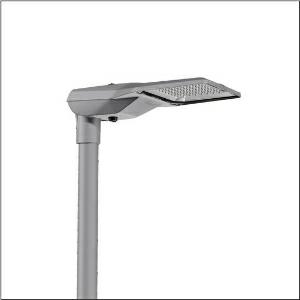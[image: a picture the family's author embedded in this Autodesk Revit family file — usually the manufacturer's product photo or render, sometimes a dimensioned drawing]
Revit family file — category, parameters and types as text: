
# Revit family: streetlight_sl_21_midi___st0_8a_5xe3c43t08lb_a4d4
name_source: partatom
category: Lighting Fixtures
units: mm (PartAtom-declared; Revit-internal decimal feet)

## family parameters
Cut with Voids When Loaded = No
Host = Face
Light Source = No
Part Type = Normal
Room Calculation Point = No
Round Connector Dimension = Use Diameter
Shared = No

## types (1)
- --- (1 x LED, 14950 lm, 99.6 W, 4000K)
    Apparent Load = 100 VA
    CIE Flux Codes = 38 75 97 100 100
    Color Rendering = 70
    Color Temperature = 4000K
    Default Elevation = 1800 mm
    Description = Streetlight SL 21 midi, mast luminaire, primary light control with lens, of PMMA, primary optical cover: cover, of toughened safety glass, transparent, light distribution: ST0.8a, light emission: direct distribution, primary light characteristic: asymmetric, installation type: side-entry, post-top, LED, High Power LED, rated luminous flux: 14.950lm, luminous efficacy: 150lm/W, light colour: 740, colour temperature: 4000K, control gear: D4i, control: overheat protection, constant luminous flux control, time-dependent luminous flux control, flexible luminous flux parameterisation, pre-setting: logarithmic dimming characteristic, mains connection: 230..240V, AC, 50/60Hz, start of lifetime: 100W, end of service life: 102W, reduction: 46W, luminaire housing, of diecast aluminium, powder-coated, Siteco® metallic grey (DB 702S), corrosivity category C5 mid according to DIN EN ISO 12944, please order mast flange separately, inclination adjustable: 0°, 5°, 10°, 15°, sealing non-destructively replaceable, multi-level sealing system, length: 644mm, width: 335mm, height: 110mm, mast flange for spigot size: 42mm (side-entry): 5XC10008XM4, 60/48mm (side-entry/post-top): 5XC10108XM2, 76/60mm (side-entry/post-top): 5XC10108XM1, mounting height: 4..8m, Smart Interface below and above, protection rating (complete): IP66, insulation class (complete): insulation class II (safety insulation), certification: CE, ENEC, ENEC+, VDE, impact resistance: IK10, permissible operating ambient temperature for outdoor applications: -40..+50°C, standard-compliant lighting for roads and squares, packaging unit: 1 piece

Light Distribution: ST0.8a
    Height = 111 mm
    Lamp = 1 x LED
    Lamp Light Flux = 14950 lm
    Lamp Power = 99.6 W
    Lamp count = 1
    Length = 644 mm
    Luminous efficacy = 150 lm/W
    Manufacturer = Siteco
    ModVariant = No
    Model = 5XE3C43T08LB
    Number of Poles = 1
    OnlyDefault = Yes
    Power Factor = 1
    Product Name = Streetlight SL 21 midi | ST0.8a
    Product group = mast luminaire | pylon top
    ProductGroupID = 6100
    Protection Class = Protection class II
    Protection Degree = IP 66
    RLX_Detail_Level = 1
    RLX_Emergency_Light_Flux = 0 lm
    RLX_Emergency_Type = 0
    RLX_Emergency_Type_DB = No
    RlxData = <blob elided: 26957 chars, md5=c2792af1>
    Socket = socket
    Standby Power = 0 W
    System Light Flux = 14950 lm
    System Power = 100 W
    Type Comments = factory setting: luminous flux: 100 % | dim-lin: 254 | 1020 mA
    Type Image = l_1004304.jpg
    URL = http://relux.com
    VarID = @adj_011377
    Voltage = 0 V
    Weight = 0.00 kg
    Width = 336 mm

## geometry (parser evidence)
native form markers: Blend x4, Sweep x13
no freeform markers — native parametric forms only
